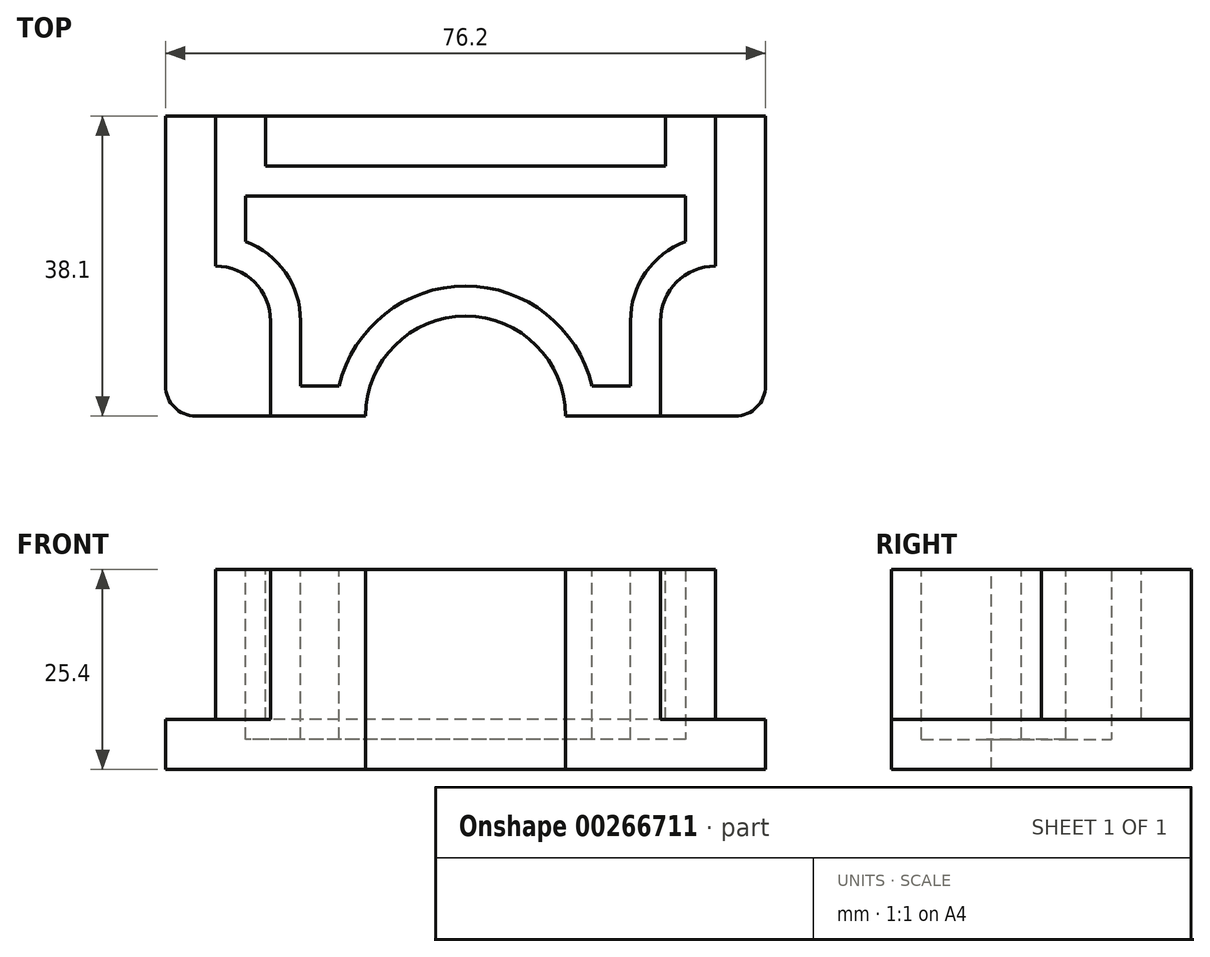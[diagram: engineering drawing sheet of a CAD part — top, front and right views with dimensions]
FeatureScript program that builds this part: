
annotation { "Feature Type Name" : "Feature", "Feature Type Description" : "" }
export const myFeature = defineFeature(function(context is Context, id is Id, definition is map)
    precondition{}
    {
        {
            var Q0;
            Q0=qCreatedBy(makeId("Top.planeOp"),FACE);
            var sketch = newSketch(context, id + "F0", { "sketchPlane" : qUnion([Q0])});
            skLineSegment(sketch, "E0.bottom", {"start": v(38.1, 19.05) * mm, "end": v(-38.1, 19.05) * mm});
            skLineSegment(sketch, "E0.top", {"start": v(38.1, -19.05) * mm, "end": v(-38.1, -19.05) * mm});
            skLineSegment(sketch, "E0.left", {"start": v(38.1, 19.05) * mm, "end": v(38.1, -19.05) * mm});
            skLineSegment(sketch, "E0.right", {"start": v(-38.1, 19.05) * mm, "end": v(-38.1, -19.05) * mm});
            skPoint(sketch, "E0.middle", {"position": v(0, 0) * mm});
            skSolve(sketch);
        }
        {
            var Q0;
            Q0=makeQuery(id+"F0.imprint","IMPRINT",FACE,{"disambiguationData":[TD([[makeQuery(id+"F0.imprint","IMPRINT",EDGE,{"derivedFrom":sQuery(id+"F0.wireOp",EDGE,"E0.bottom")}),1.0]])]});
            extrude(context, id + "F1", {"entities" : qUnion([Q0]), "depth" : 25.4 * mm});
        }
        {
            var Q0;
            Q0=makeQuery(id+"F1.opExtrude","CAP_FACE",FACE,{"disambiguationData":[OSD([sQuery(id+"F0.wireOp",EDGE,"E0.bottom"),sQuery(id+"F0.wireOp",EDGE,"E0.top"),sQuery(id+"F0.wireOp",EDGE,"E0.left"),sQuery(id+"F0.wireOp",EDGE,"E0.right")])],"isStart":false});
            var sketch = newSketch(context, id + "F2", { "sketchPlane" : qUnion([Q0])});
            skLineSegment(sketch, "E1.bottom", {"start": v(-25.4, 19.05) * mm, "end": v(25.4, 19.05) * mm});
            skLineSegment(sketch, "E1.top", {"start": v(-25.4, 12.7) * mm, "end": v(25.4, 12.7) * mm});
            skLineSegment(sketch, "E1.left", {"start": v(-25.4, 19.05) * mm, "end": v(-25.4, 12.7) * mm});
            skLineSegment(sketch, "E1.right", {"start": v(25.4, 19.05) * mm, "end": v(25.4, 12.7) * mm});
            skSolve(sketch);
        }
        {
            var Q0;
            Q0=makeQuery(id+"F2.imprint","IMPRINT",FACE,{"disambiguationData":[TD([[makeQuery(id+"F2.imprint","IMPRINT",EDGE,{"derivedFrom":sQuery(id+"F2.wireOp",EDGE,"E1.bottom")}),1.0]])]});
            extrude(context, id + "F3", {"entities" : qUnion([Q0]), "operationType" : NewBodyOperationType.REMOVE, "oppositeDirection" : true, "depth" : 19.05 * mm});
        }
        {
            var Q0;
            Q0=makeQuery(id+"F1.opExtrude","CAP_FACE",FACE,{"disambiguationData":[OSD([sQuery(id+"F0.wireOp",EDGE,"E0.bottom"),sQuery(id+"F0.wireOp",EDGE,"E0.top"),sQuery(id+"F0.wireOp",EDGE,"E0.left"),sQuery(id+"F0.wireOp",EDGE,"E0.right")])],"isStart":false});
            var sketch = newSketch(context, id + "F4", { "sketchPlane" : qUnion([Q0])});
            skLineSegment(sketch, "E2.bottom", {"start": v(-38.1, 19.05) * mm, "end": v(-31.75, 19.05) * mm});
            skLineSegment(sketch, "E2.top", {"start": v(-38.1, -19.05) * mm, "end": v(-31.75, -19.05) * mm});
            skLineSegment(sketch, "E2.left", {"start": v(-38.1, 19.05) * mm, "end": v(-38.1, -19.05) * mm});
            skLineSegment(sketch, "E2.right", {"start": v(-31.75, 19.05) * mm, "end": v(-31.75, -19.05) * mm});
            skLineSegment(sketch, "E3.bottom", {"start": v(38.1, 19.05) * mm, "end": v(31.75, 19.05) * mm});
            skLineSegment(sketch, "E3.top", {"start": v(38.1, -19.05) * mm, "end": v(31.75, -19.05) * mm});
            skLineSegment(sketch, "E3.left", {"start": v(38.1, 19.05) * mm, "end": v(38.1, -19.05) * mm});
            skLineSegment(sketch, "E3.right", {"start": v(31.75, 19.05) * mm, "end": v(31.75, -19.05) * mm});
            skSolve(sketch);
        }
        {
            var Q0;
            Q0=makeQuery(id+"F4.imprint","IMPRINT",FACE,{"disambiguationData":[TD([[makeQuery(id+"F4.imprint","IMPRINT",EDGE,{"derivedFrom":sQuery(id+"F4.wireOp",EDGE,"E2.bottom")}),1.0]])]});
            var Q1;
            Q1=makeQuery(id+"F4.imprint","IMPRINT",FACE,{"disambiguationData":[TD([[makeQuery(id+"F4.imprint","IMPRINT",EDGE,{"derivedFrom":sQuery(id+"F4.wireOp",EDGE,"E3.bottom")}),1.0]])]});
            extrude(context, id + "F5", {"entities" : qUnion([Q0, Q1]), "operationType" : NewBodyOperationType.REMOVE, "oppositeDirection" : true, "depth" : 19.05 * mm});
        }
        {
            var Q0;
            Q0=makeQuery(id+"F1.opExtrude","CAP_FACE",FACE,{"disambiguationData":[OSD([sQuery(id+"F0.wireOp",EDGE,"E0.bottom"),sQuery(id+"F0.wireOp",EDGE,"E0.top"),sQuery(id+"F0.wireOp",EDGE,"E0.left"),sQuery(id+"F0.wireOp",EDGE,"E0.right")])],"isStart":false});
            var sketch = newSketch(context, id + "F6", { "sketchPlane" : qUnion([Q0])});
            skCircle(sketch, "E4", {"center": v(0, -19.05) * mm, "radius": 12.7 * mm});
            skSolve(sketch);
        }
        {
            var Q0;
            {var subQ0=sQuery(id+"F6.wireOp",EDGE,"E4");var subQ1=makeQuery(id+"F1.opExtrude","CAP_EDGE",EDGE,{"disambiguationData":[OSD([sQuery(id+"F0.wireOp",EDGE,"E0.top")])],"isStart":false});var subQ2=makeQuery(id+"F6.imprint","INTERSECT",VERTEX,{"disambiguationData":[OD(0.0)],"derivedFrom":[subQ1,subQ0]});Q0=makeQuery(id+"F6.imprint","IMPRINT",FACE,{"disambiguationData":[TD([[makeQuery(id+"F6.imprint","IMPRINT",EDGE,{"disambiguationData":[TD([[subQ2,1.0]])],"derivedFrom":subQ0}),1.0]])]});}
            extrude(context, id + "F7", {"entities" : qUnion([Q0]), "operationType" : NewBodyOperationType.REMOVE, "oppositeDirection" : true, "depth" : 25.4 * mm});
        }
        {
            var Q0;
            Q0=makeQuery(id+"F1.opExtrude","SWEPT_EDGE",EDGE,{"disambiguationData":[OSD([sQuery(id+"F0.wireOp",EDGE,"E0.top"),sQuery(id+"F0.wireOp",EDGE,"E0.left")])]});
            var Q1;
            Q1=makeQuery(id+"F1.opExtrude","SWEPT_EDGE",EDGE,{"disambiguationData":[OSD([sQuery(id+"F0.wireOp",EDGE,"E0.top"),sQuery(id+"F0.wireOp",EDGE,"E0.right")])]});
            fillet(context, id + "F8", {"entities" : qUnion([Q0, Q1]), "radius" : 3.8 * mm, "tangentPropagation" : true, "allowEdgeOverflow" : false});
        }
        {
            var Q0;
            Q0=makeQuery(id+"F1.opExtrude","CAP_FACE",FACE,{"disambiguationData":[OSD([sQuery(id+"F0.wireOp",EDGE,"E0.bottom"),sQuery(id+"F0.wireOp",EDGE,"E0.top"),sQuery(id+"F0.wireOp",EDGE,"E0.left"),sQuery(id+"F0.wireOp",EDGE,"E0.right")])],"isStart":false});
            var sketch = newSketch(context, id + "F9", { "sketchPlane" : qUnion([Q0])});
            skLineSegment(sketch, "E5.bottom", {"start": v(31.75, -19.05) * mm, "end": v(24.76, -19.05) * mm});
            skLineSegment(sketch, "E5.top", {"start": v(31.75, 0) * mm, "end": v(24.76, 0) * mm});
            skLineSegment(sketch, "E5.left", {"start": v(31.75, -19.05) * mm, "end": v(31.75, 0) * mm});
            skLineSegment(sketch, "E5.right", {"start": v(24.76, -19.05) * mm, "end": v(24.76, 0) * mm});
            skLineSegment(sketch, "E6.bottom", {"start": v(-31.75, -19.05) * mm, "end": v(-24.77, -19.05) * mm});
            skLineSegment(sketch, "E6.top", {"start": v(-31.75, 0) * mm, "end": v(-24.77, 0) * mm});
            skLineSegment(sketch, "E6.left", {"start": v(-31.75, -19.05) * mm, "end": v(-31.75, 0) * mm});
            skLineSegment(sketch, "E6.right", {"start": v(-24.77, -19.05) * mm, "end": v(-24.77, 0) * mm});
            skSolve(sketch);
        }
        {
            var Q0;
            Q0=makeQuery(id+"F9.imprint","IMPRINT",FACE,{"disambiguationData":[TD([[makeQuery(id+"F9.imprint","IMPRINT",EDGE,{"derivedFrom":sQuery(id+"F9.wireOp",EDGE,"E6.bottom")}),-1.0]])]});
            var Q1;
            Q1=makeQuery(id+"F9.imprint","IMPRINT",FACE,{"disambiguationData":[TD([[makeQuery(id+"F9.imprint","IMPRINT",EDGE,{"derivedFrom":sQuery(id+"F9.wireOp",EDGE,"E5.bottom")}),-1.0]])]});
            extrude(context, id + "F10", {"entities" : qUnion([Q0, Q1]), "operationType" : NewBodyOperationType.REMOVE, "oppositeDirection" : true, "depth" : 19.05 * mm});
        }
        {
            var Q0;
            Q0=makeQuery(id+"F10.boolean.opBoolean","COPY",EDGE,{"derivedFrom":makeQuery(id+"F10.opExtrude","SWEPT_EDGE",EDGE,{"disambiguationData":[OSD([sQuery(id+"F9.wireOp",EDGE,"E5.top"),sQuery(id+"F9.wireOp",EDGE,"E5.right")])]})});
            var Q1;
            Q1=makeQuery(id+"F10.boolean.opBoolean","COPY",EDGE,{"derivedFrom":makeQuery(id+"F10.opExtrude","SWEPT_EDGE",EDGE,{"disambiguationData":[OSD([sQuery(id+"F9.wireOp",EDGE,"E6.top"),sQuery(id+"F9.wireOp",EDGE,"E6.right")])]})});
            fillet(context, id + "F11", {"entities" : qUnion([Q0, Q1]), "radius" : 7 * mm, "tangentPropagation" : true, "allowEdgeOverflow" : false});
        }
        {
            var Q0;
            Q0=makeQuery(id+"F1.opExtrude","CAP_FACE",FACE,{"disambiguationData":[OSD([sQuery(id+"F0.wireOp",EDGE,"E0.bottom"),sQuery(id+"F0.wireOp",EDGE,"E0.top"),sQuery(id+"F0.wireOp",EDGE,"E0.left"),sQuery(id+"F0.wireOp",EDGE,"E0.right")])],"isStart":false});
            shell(context, id + "F12", {"entities" : qUnion([Q0]), "thickness" : 3.8 * mm});
        }
    });
